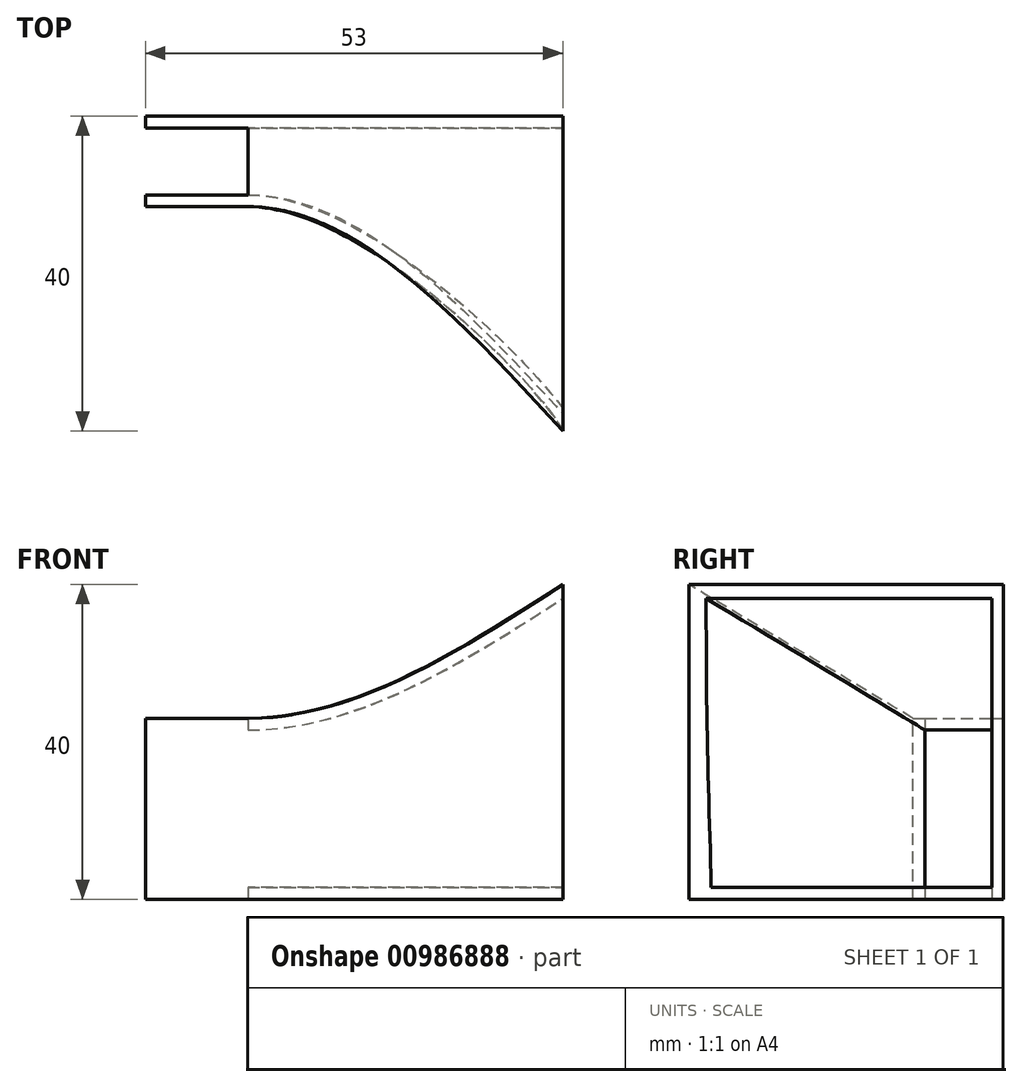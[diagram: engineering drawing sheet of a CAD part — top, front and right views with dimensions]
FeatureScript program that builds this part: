
annotation { "Feature Type Name" : "Feature", "Feature Type Description" : "" }
export const myFeature = defineFeature(function(context is Context, id is Id, definition is map)
    precondition{}
    {
        {
            var Q0;
            Q0=qCreatedBy(makeId("Top.planeOp"),FACE);
            var sketch = newSketch(context, id + "F0", { "sketchPlane" : qUnion([Q0])});
            skLineSegment(sketch, "E0", {"start": v(0, 0) * mm, "end": v(40, 0) * mm});
            skLineSegment(sketch, "E1", {"start": v(40, 0) * mm, "end": v(40, -40) * mm});
            skLineSegment(sketch, "E2", {"start": v(0, 0) * mm, "end": v(0, -11.5) * mm});
            skFitSpline(sketch, "E3", {"points": [v(0, -11.5) * mm, v(40, -40) * mm], "startDerivative": vector(46.54, 0) * mm, "endDerivative": vector(5.17, -12.9) * mm});
            skSolve(sketch);
        }
        {
            var Q0;
            Q0=qCreatedBy(makeId("Right.planeOp"),FACE);
            var Q1;
            Q1=sQuery(id+"F0.wireOp",EDGE,"E1");
            cPlane(context, id + "F1", {"entities" : qUnion([Q0, Q1]), "cplaneType" : CPlaneType.LINE_ANGLE, "offset" : 25 * mm, "angle" : 0 * degree, "width" : 150 * mm, "height" : 150 * mm});
        }
        {
            var Q0;
            Q0=qCreatedBy(id+"F1.planeOp",FACE);
            var sketch = newSketch(context, id + "F2", { "sketchPlane" : qUnion([Q0])});
            skLineSegment(sketch, "E4.0", {"start": v(0, 0) * mm, "end": v(40, 0) * mm});
            skLineSegment(sketch, "E5", {"start": v(40, 0) * mm, "end": v(40, 40) * mm});
            skLineSegment(sketch, "E6", {"start": v(40, 40) * mm, "end": v(0, 40) * mm});
            skLineSegment(sketch, "E7", {"start": v(0, 40) * mm, "end": v(0, 0) * mm});
            skSolve(sketch);
        }
        {
            var Q0;
            Q0=qCreatedBy(makeId("Right.planeOp"),FACE);
            var sketch = newSketch(context, id + "F3", { "sketchPlane" : qUnion([Q0])});
            skLineSegment(sketch, "E8.0", {"start": v(0, 0) * mm, "end": v(-11.5, 0) * mm});
            skLineSegment(sketch, "E9", {"start": v(-11.5, 0) * mm, "end": v(-11.5, 23) * mm});
            skLineSegment(sketch, "E10", {"start": v(-11.5, 23) * mm, "end": v(0, 23) * mm});
            skLineSegment(sketch, "E11", {"start": v(0, 23) * mm, "end": v(0, 0) * mm});
            skSolve(sketch);
        }
        {
            var Q0;
            Q0=makeQuery(id+"F3.imprint","IMPRINT",FACE,{"disambiguationData":[TD([[makeQuery(id+"F3.imprint","IMPRINT",EDGE,{"derivedFrom":sQuery(id+"F3.wireOp",EDGE,"E8.0")}),-1.0]])]});
            var Q1;
            Q1=makeQuery(id+"F2.imprint","IMPRINT",FACE,{"disambiguationData":[TD([[makeQuery(id+"F2.imprint","IMPRINT",EDGE,{"derivedFrom":sQuery(id+"F2.wireOp",EDGE,"E4.0")}),1.0]])]});
            var Q2;
            Q2=sQuery(id+"F0.wireOp",EDGE,"E0");
            var Q3;
            Q3=sQuery(id+"F0.wireOp",EDGE,"E3");
            loft(context, id + "F4", {"addGuides" : true, "startCondition" : LoftEndDerivativeType.NORMAL_TO_PROFILE, "startMagnitude" : 1, "sheetProfilesArray" : [{ "sheetProfileEntities" : qUnion([Q0]) }, { "sheetProfileEntities" : qUnion([Q1]) }], "guidesArray" : [{ "guideEntities" : qUnion([Q2]), "guideDerivativeType" : LoftGuideDerivativeType.DEFAULT, "guideDerivativeMagnitude" : 1 }, { "guideEntities" : qUnion([Q3]), "guideDerivativeType" : LoftGuideDerivativeType.DEFAULT, "guideDerivativeMagnitude" : 1 }]});
        }
        {
            var Q0;
            Q0=makeQuery(id+"F4.opLoft","CAP_FACE",FACE,{"disambiguationData":[OSD([makeQuery(id+"F2.imprint","IMPRINT",FACE,{"disambiguationData":[TD([[makeQuery(id+"F2.imprint","IMPRINT",EDGE,{"derivedFrom":sQuery(id+"F2.wireOp",EDGE,"E4.0")}),1.0]])]})])],"isStart":true});
            var Q1;
            Q1=makeQuery(id+"F4.opLoft","CAP_FACE",FACE,{"disambiguationData":[OSD([makeQuery(id+"F3.imprint","IMPRINT",FACE,{"disambiguationData":[TD([[makeQuery(id+"F3.imprint","IMPRINT",EDGE,{"derivedFrom":sQuery(id+"F3.wireOp",EDGE,"E8.0")}),-1.0]])]})])],"isStart":true});
            shell(context, id + "F5", {"entities" : qUnion([Q0, Q1]), "thickness" : 1.5 * mm});
        }
        {
            var Q0;
            Q0=makeQuery(id+"F4.opLoft","CAP_FACE",FACE,{"disambiguationData":[OSD([makeQuery(id+"F3.imprint","IMPRINT",FACE,{"disambiguationData":[TD([[makeQuery(id+"F3.imprint","IMPRINT",EDGE,{"derivedFrom":sQuery(id+"F3.wireOp",EDGE,"E8.0")}),-1.0]])]})])],"isStart":true});
            var sketch = newSketch(context, id + "F6", { "sketchPlane" : qUnion([Q0])});
            skLineSegment(sketch, "E12.0", {"start": v(11.5, 23) * mm, "end": v(11.5, 0) * mm});
            skLineSegment(sketch, "E12.1", {"start": v(0, 0) * mm, "end": v(0, 23) * mm});
            skLineSegment(sketch, "E13.0", {"start": v(1.5, 1.5) * mm, "end": v(1.5, 21.5) * mm, "construction": true});
            skFitSpline(sketch, "E13.1", {"points": [v(10, 21.5) * mm, v(10, 14.83) * mm, v(10, 8.17) * mm, v(10, 1.5) * mm], "construction": true});
            skLineSegment(sketch, "E14", {"start": v(1.5, 23) * mm, "end": v(1.5, 0) * mm});
            skLineSegment(sketch, "E15", {"start": v(1.5, 0) * mm, "end": v(0, 0) * mm});
            skLineSegment(sketch, "E16", {"start": v(0, 23) * mm, "end": v(1.5, 23) * mm});
            skLineSegment(sketch, "E17", {"start": v(10, 23) * mm, "end": v(10, 0) * mm});
            skLineSegment(sketch, "E18", {"start": v(10, 0) * mm, "end": v(11.5, 0) * mm});
            skLineSegment(sketch, "E19", {"start": v(10, 23) * mm, "end": v(11.5, 23) * mm});
            skSolve(sketch);
        }
        {
            var Q0;
            Q0=makeQuery(id+"F6.imprint","IMPRINT",FACE,{"disambiguationData":[TD([[makeQuery(id+"F6.imprint","IMPRINT",EDGE,{"derivedFrom":sQuery(id+"F6.wireOp",EDGE,"E12.0")}),-1.0]])]});
            var Q1;
            Q1=makeQuery(id+"F6.imprint","IMPRINT",FACE,{"disambiguationData":[TD([[makeQuery(id+"F6.imprint","IMPRINT",EDGE,{"derivedFrom":sQuery(id+"F6.wireOp",EDGE,"E12.1")}),-1.0]])]});
            extrude(context, id + "F7", {"entities" : qUnion([Q0, Q1]), "operationType" : NewBodyOperationType.ADD, "depth" : 13 * mm, "offsetDistance" : 25 * mm});
        }
    });
